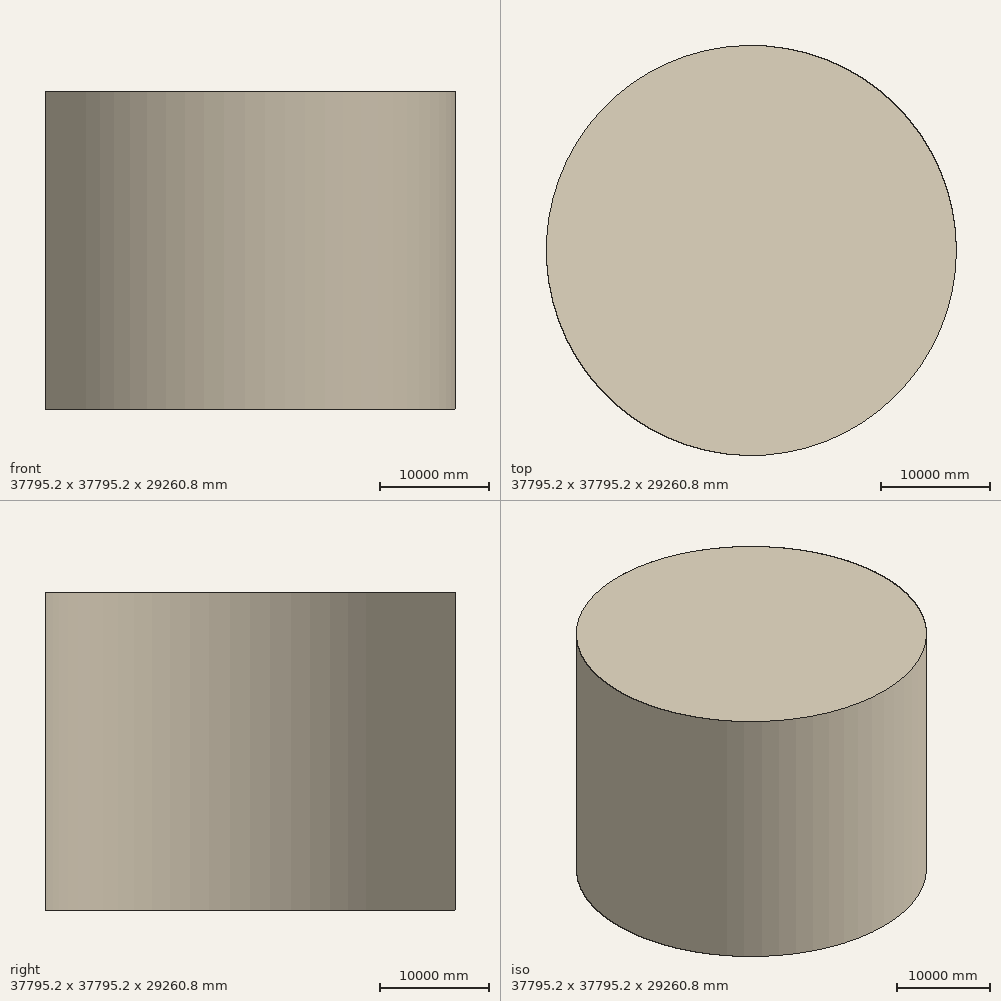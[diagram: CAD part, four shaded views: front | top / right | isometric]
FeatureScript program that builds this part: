
annotation { "Feature Type Name" : "Feature", "Feature Type Description" : "" }
export const myFeature = defineFeature(function(context is Context, id is Id, definition is map)
    precondition{}
    {
        {
            var Q0;
            Q0=qCreatedBy(makeId("Top.planeOp"),FACE);
            var sketch = newSketch(context, id + "F0", { "sketchPlane" : qUnion([Q0])});
            skCircle(sketch, "E0", {"center": v(0, 0) * mm, "radius": 18897.6 * mm});
            skSolve(sketch);
        }
        {
            var Q0;
            Q0=makeQuery(id+"F0.imprint","IMPRINT",FACE,{"disambiguationData":[TD([[makeQuery(id+"F0.imprint","IMPRINT",EDGE,{"derivedFrom":sQuery(id+"F0.wireOp",EDGE,"E0")}),1.0]])]});
            extrude(context, id + "F1", {"entities" : qUnion([Q0]), "depth" : 29260.8 * mm, "offsetDistance" : 25 * mm});
        }
    });
